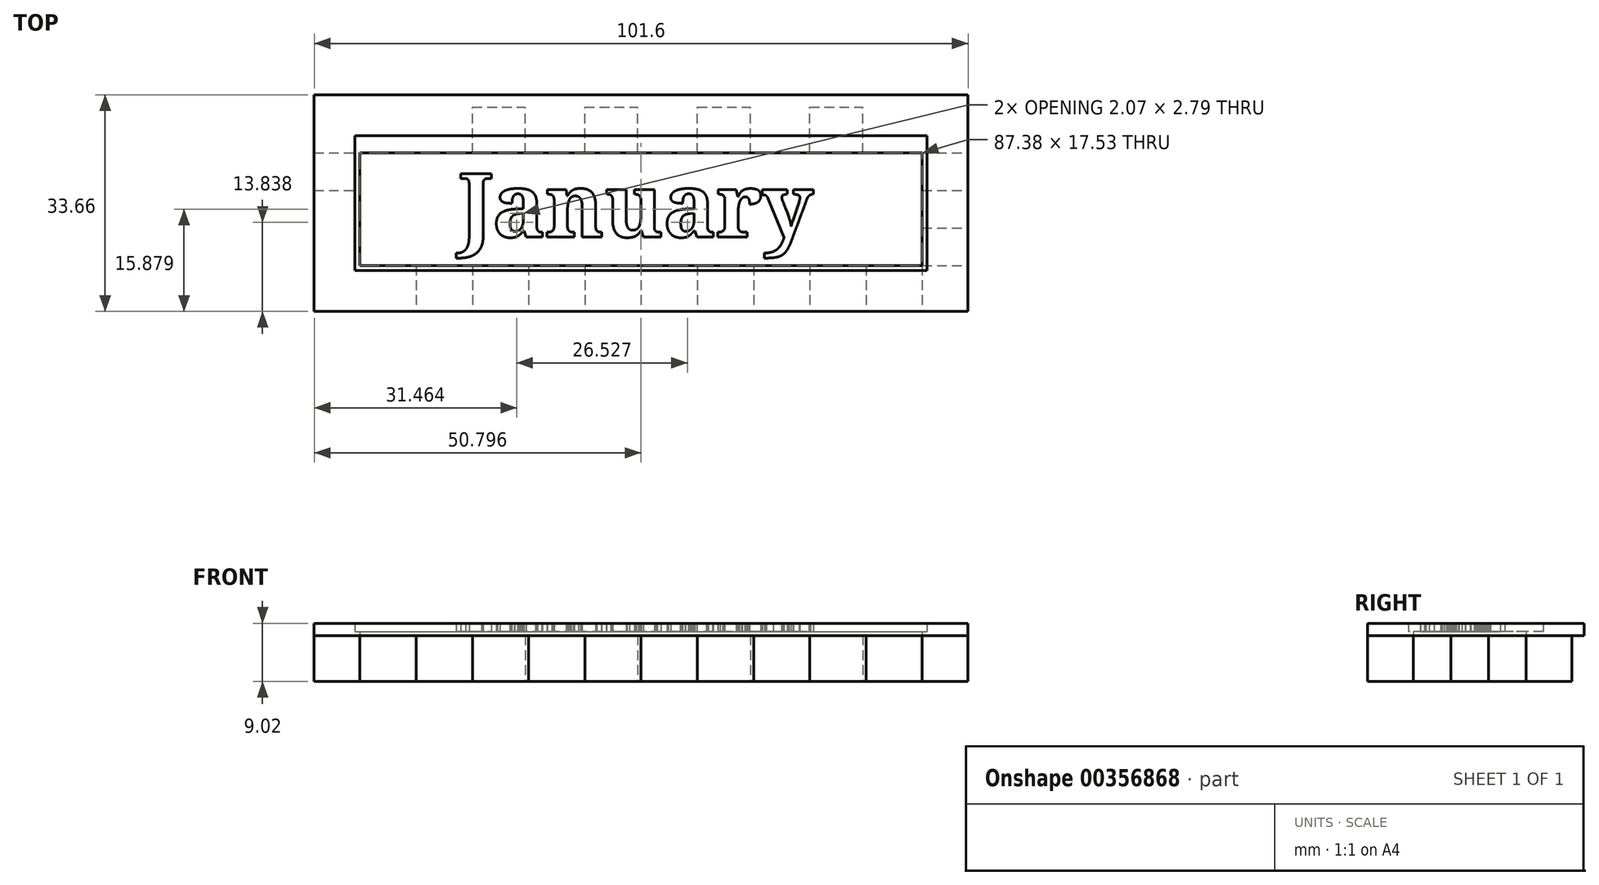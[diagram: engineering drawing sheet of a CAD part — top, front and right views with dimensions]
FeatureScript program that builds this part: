
annotation { "Feature Type Name" : "Feature", "Feature Type Description" : "" }
export const myFeature = defineFeature(function(context is Context, id is Id, definition is map)
    precondition{}
    {
        {
            var Q0;
            Q0=qCreatedBy(makeId("Top.planeOp"),FACE);
            var sketch = newSketch(context, id + "F0", { "sketchPlane" : qUnion([Q0])});
            skLineSegment(sketch, "E0.bottom", {"start": v(-52.12, 11.37) * mm, "end": v(49.48, 11.37) * mm});
            skLineSegment(sketch, "E0.top", {"start": v(-52.12, -20.38) * mm, "end": v(49.48, -20.38) * mm});
            skLineSegment(sketch, "E0.left", {"start": v(-52.12, 11.37) * mm, "end": v(-52.12, -20.38) * mm});
            skLineSegment(sketch, "E0.right", {"start": v(49.48, 11.37) * mm, "end": v(49.48, -20.38) * mm});
            skLineSegment(sketch, "E1.bottom", {"start": v(-52.12, 11.37) * mm, "end": v(-45.01, 11.37) * mm});
            skLineSegment(sketch, "E1.top", {"start": v(-52.12, 4.26) * mm, "end": v(-45.01, 4.26) * mm});
            skLineSegment(sketch, "E1.left", {"start": v(-52.12, 11.37) * mm, "end": v(-52.12, 4.26) * mm});
            skLineSegment(sketch, "E1.right", {"start": v(-45.01, 11.37) * mm, "end": v(-45.01, 4.26) * mm});
            skLineSegment(sketch, "E2.bottom", {"start": v(-45.01, 11.37) * mm, "end": v(-36.78, 11.37) * mm});
            skLineSegment(sketch, "E2.top", {"start": v(-45.01, 4.26) * mm, "end": v(-36.78, 4.26) * mm});
            skLineSegment(sketch, "E2.right", {"start": v(-36.78, 11.37) * mm, "end": v(-36.78, 4.26) * mm});
            skLineSegment(sketch, "E3.bottom", {"start": v(-36.78, 4.26) * mm, "end": v(-27.54, 4.26) * mm});
            skLineSegment(sketch, "E3.top", {"start": v(-36.78, 11.37) * mm, "end": v(-27.54, 11.37) * mm});
            skLineSegment(sketch, "E3.left", {"start": v(-36.78, 4.26) * mm, "end": v(-36.78, 11.37) * mm});
            skLineSegment(sketch, "E3.right", {"start": v(-27.54, 4.26) * mm, "end": v(-27.54, 11.37) * mm});
            skLineSegment(sketch, "E4.bottom", {"start": v(-27.54, 4.26) * mm, "end": v(-19.3, 4.26) * mm});
            skLineSegment(sketch, "E4.top", {"start": v(-27.54, 11.37) * mm, "end": v(-19.3, 11.37) * mm});
            skLineSegment(sketch, "E4.right", {"start": v(-19.3, 4.26) * mm, "end": v(-19.3, 11.37) * mm});
            skLineSegment(sketch, "E5.bottom", {"start": v(-19.3, 4.26) * mm, "end": v(-10.06, 4.26) * mm});
            skLineSegment(sketch, "E5.top", {"start": v(-19.3, 11.37) * mm, "end": v(-10.06, 11.37) * mm});
            skLineSegment(sketch, "E5.right", {"start": v(-10.06, 4.26) * mm, "end": v(-10.06, 11.37) * mm});
            skLineSegment(sketch, "E6.bottom", {"start": v(-10.06, 4.26) * mm, "end": v(-10.06, 4.26) * mm});
            skLineSegment(sketch, "E6.top", {"start": v(-10.06, 11.37) * mm, "end": v(-10.06, 11.37) * mm});
            skLineSegment(sketch, "E7.bottom", {"start": v(-10.06, 4.26) * mm, "end": v(-1.83, 4.26) * mm});
            skLineSegment(sketch, "E7.top", {"start": v(-10.06, 11.37) * mm, "end": v(-1.83, 11.37) * mm});
            skLineSegment(sketch, "E7.right", {"start": v(-1.83, 4.26) * mm, "end": v(-1.83, 11.37) * mm});
            skLineSegment(sketch, "E8.bottom", {"start": v(-1.83, 4.26) * mm, "end": v(7.41, 4.26) * mm});
            skLineSegment(sketch, "E8.top", {"start": v(-1.83, 11.37) * mm, "end": v(7.41, 11.37) * mm});
            skLineSegment(sketch, "E8.right", {"start": v(7.41, 4.26) * mm, "end": v(7.41, 11.37) * mm});
            skLineSegment(sketch, "E9.bottom", {"start": v(7.41, 4.26) * mm, "end": v(15.64, 4.26) * mm});
            skLineSegment(sketch, "E9.top", {"start": v(7.41, 11.37) * mm, "end": v(15.64, 11.37) * mm});
            skLineSegment(sketch, "E9.right", {"start": v(15.64, 4.26) * mm, "end": v(15.64, 11.37) * mm});
            skLineSegment(sketch, "E10.bottom", {"start": v(15.64, 4.26) * mm, "end": v(24.89, 4.26) * mm});
            skLineSegment(sketch, "E10.top", {"start": v(15.64, 11.37) * mm, "end": v(24.89, 11.37) * mm});
            skLineSegment(sketch, "E10.right", {"start": v(24.89, 4.26) * mm, "end": v(24.89, 11.37) * mm});
            skLineSegment(sketch, "E11.bottom", {"start": v(24.89, 4.26) * mm, "end": v(24.89, 4.26) * mm});
            skLineSegment(sketch, "E11.top", {"start": v(24.89, 11.37) * mm, "end": v(24.89, 11.37) * mm});
            skLineSegment(sketch, "E12.bottom", {"start": v(24.89, 4.26) * mm, "end": v(33.12, 4.26) * mm});
            skLineSegment(sketch, "E12.top", {"start": v(24.89, 11.37) * mm, "end": v(33.12, 11.37) * mm});
            skLineSegment(sketch, "E12.right", {"start": v(33.12, 4.26) * mm, "end": v(33.12, 11.37) * mm});
            skLineSegment(sketch, "E13.bottom", {"start": v(33.12, 4.26) * mm, "end": v(42.36, 4.26) * mm});
            skLineSegment(sketch, "E13.top", {"start": v(33.12, 11.37) * mm, "end": v(42.36, 11.37) * mm});
            skLineSegment(sketch, "E13.right", {"start": v(42.36, 4.26) * mm, "end": v(42.36, 11.37) * mm});
            skLineSegment(sketch, "E14.bottom", {"start": v(42.36, 4.26) * mm, "end": v(49.48, 4.26) * mm});
            skLineSegment(sketch, "E14.top", {"start": v(42.36, 11.37) * mm, "end": v(49.48, 11.37) * mm});
            skLineSegment(sketch, "E14.right", {"start": v(49.48, 4.26) * mm, "end": v(49.48, 11.37) * mm});
            skLineSegment(sketch, "E15.bottom", {"start": v(-52.12, -20.38) * mm, "end": v(-45.01, -20.38) * mm});
            skLineSegment(sketch, "E15.top", {"start": v(-52.12, -13.26) * mm, "end": v(-45.01, -13.26) * mm});
            skLineSegment(sketch, "E15.left", {"start": v(-52.12, -20.38) * mm, "end": v(-52.12, -13.26) * mm});
            skLineSegment(sketch, "E15.right", {"start": v(-45.01, -20.38) * mm, "end": v(-45.01, -13.26) * mm});
            skLineSegment(sketch, "E16.bottom", {"start": v(-45.01, -13.26) * mm, "end": v(-45.01, -13.26) * mm});
            skLineSegment(sketch, "E16.top", {"start": v(-45.01, -20.38) * mm, "end": v(-45.01, -20.38) * mm});
            skLineSegment(sketch, "E16.left", {"start": v(-45.01, -13.26) * mm, "end": v(-45.01, -20.38) * mm});
            skLineSegment(sketch, "E16.right", {"start": v(-45.01, -13.26) * mm, "end": v(-45.01, -20.38) * mm});
            skLineSegment(sketch, "E17.bottom", {"start": v(-45.01, -13.26) * mm, "end": v(-36.27, -13.26) * mm});
            skLineSegment(sketch, "E17.top", {"start": v(-45.01, -20.38) * mm, "end": v(-36.27, -20.38) * mm});
            skLineSegment(sketch, "E17.right", {"start": v(-36.27, -13.26) * mm, "end": v(-36.27, -20.38) * mm});
            skLineSegment(sketch, "E18.bottom", {"start": v(-36.27, -13.26) * mm, "end": v(-36.27, -13.26) * mm});
            skLineSegment(sketch, "E18.top", {"start": v(-36.27, -20.38) * mm, "end": v(-36.27, -20.38) * mm});
            skLineSegment(sketch, "E19.bottom", {"start": v(-36.27, -13.26) * mm, "end": v(-27.54, -13.26) * mm});
            skLineSegment(sketch, "E19.top", {"start": v(-36.27, -20.38) * mm, "end": v(-27.54, -20.38) * mm});
            skLineSegment(sketch, "E19.right", {"start": v(-27.54, -13.26) * mm, "end": v(-27.54, -20.38) * mm});
            skLineSegment(sketch, "E20.bottom", {"start": v(-27.54, -13.26) * mm, "end": v(-18.8, -13.26) * mm});
            skLineSegment(sketch, "E20.top", {"start": v(-27.54, -20.38) * mm, "end": v(-18.8, -20.38) * mm});
            skLineSegment(sketch, "E20.right", {"start": v(-18.8, -13.26) * mm, "end": v(-18.8, -20.38) * mm});
            skLineSegment(sketch, "E21.bottom", {"start": v(-18.8, -13.26) * mm, "end": v(-10.06, -13.26) * mm});
            skLineSegment(sketch, "E21.top", {"start": v(-18.8, -20.38) * mm, "end": v(-10.06, -20.38) * mm});
            skLineSegment(sketch, "E21.right", {"start": v(-10.06, -13.26) * mm, "end": v(-10.06, -20.38) * mm});
            skLineSegment(sketch, "E22.bottom", {"start": v(-10.06, -13.26) * mm, "end": v(-1.32, -13.26) * mm});
            skLineSegment(sketch, "E22.top", {"start": v(-10.06, -20.38) * mm, "end": v(-1.32, -20.38) * mm});
            skLineSegment(sketch, "E22.right", {"start": v(-1.32, -13.26) * mm, "end": v(-1.32, -20.38) * mm});
            skLineSegment(sketch, "E23.bottom", {"start": v(-1.32, -13.26) * mm, "end": v(7.41, -13.26) * mm});
            skLineSegment(sketch, "E23.top", {"start": v(-1.32, -20.38) * mm, "end": v(7.41, -20.38) * mm});
            skLineSegment(sketch, "E23.right", {"start": v(7.41, -13.26) * mm, "end": v(7.41, -20.38) * mm});
            skLineSegment(sketch, "E24.bottom", {"start": v(7.41, -13.26) * mm, "end": v(16.15, -13.26) * mm});
            skLineSegment(sketch, "E24.top", {"start": v(7.41, -20.38) * mm, "end": v(16.15, -20.38) * mm});
            skLineSegment(sketch, "E24.right", {"start": v(16.15, -13.26) * mm, "end": v(16.15, -20.38) * mm});
            skLineSegment(sketch, "E25.bottom", {"start": v(16.15, -13.26) * mm, "end": v(24.89, -13.26) * mm});
            skLineSegment(sketch, "E25.top", {"start": v(16.15, -20.38) * mm, "end": v(24.89, -20.38) * mm});
            skLineSegment(sketch, "E25.right", {"start": v(24.89, -13.26) * mm, "end": v(24.89, -20.38) * mm});
            skLineSegment(sketch, "E26.bottom", {"start": v(24.89, -13.26) * mm, "end": v(33.63, -13.26) * mm});
            skLineSegment(sketch, "E26.top", {"start": v(24.89, -20.38) * mm, "end": v(33.63, -20.38) * mm});
            skLineSegment(sketch, "E26.right", {"start": v(33.63, -13.26) * mm, "end": v(33.63, -20.38) * mm});
            skLineSegment(sketch, "E27.bottom", {"start": v(33.63, -13.26) * mm, "end": v(42.36, -13.26) * mm});
            skLineSegment(sketch, "E27.top", {"start": v(33.63, -20.38) * mm, "end": v(42.36, -20.38) * mm});
            skLineSegment(sketch, "E27.right", {"start": v(42.36, -13.26) * mm, "end": v(42.36, -20.38) * mm});
            skLineSegment(sketch, "E28.bottom", {"start": v(42.36, -13.26) * mm, "end": v(49.48, -13.26) * mm});
            skLineSegment(sketch, "E28.top", {"start": v(42.36, -20.38) * mm, "end": v(49.48, -20.38) * mm});
            skLineSegment(sketch, "E28.right", {"start": v(49.48, -13.26) * mm, "end": v(49.48, -20.38) * mm});
            skLineSegment(sketch, "E29.top", {"start": v(-52.12, -1.58) * mm, "end": v(-45.01, -1.58) * mm});
            skLineSegment(sketch, "E29.left", {"start": v(-52.12, 4.26) * mm, "end": v(-52.12, -1.58) * mm});
            skLineSegment(sketch, "E29.right", {"start": v(-45.01, 4.26) * mm, "end": v(-45.01, -1.58) * mm});
            skLineSegment(sketch, "E30.top", {"start": v(-52.12, -7.42) * mm, "end": v(-45.01, -7.42) * mm});
            skLineSegment(sketch, "E30.left", {"start": v(-52.12, -1.58) * mm, "end": v(-52.12, -7.42) * mm});
            skLineSegment(sketch, "E30.right", {"start": v(-45.01, -1.58) * mm, "end": v(-45.01, -7.42) * mm});
            skLineSegment(sketch, "E31.bottom", {"start": v(-45.01, -7.42) * mm, "end": v(-52.12, -7.42) * mm});
            skLineSegment(sketch, "E31.top", {"start": v(-45.01, -13.26) * mm, "end": v(-52.12, -13.26) * mm});
            skLineSegment(sketch, "E31.left", {"start": v(-45.01, -7.42) * mm, "end": v(-45.01, -13.26) * mm});
            skLineSegment(sketch, "E31.right", {"start": v(-52.12, -7.42) * mm, "end": v(-52.12, -13.26) * mm});
            skLineSegment(sketch, "E32.top", {"start": v(42.36, -1.58) * mm, "end": v(49.48, -1.58) * mm});
            skLineSegment(sketch, "E32.left", {"start": v(42.36, 4.26) * mm, "end": v(42.36, -1.58) * mm});
            skLineSegment(sketch, "E32.right", {"start": v(49.48, 4.26) * mm, "end": v(49.48, -1.58) * mm});
            skLineSegment(sketch, "E33.top", {"start": v(42.36, -7.42) * mm, "end": v(49.48, -7.42) * mm});
            skLineSegment(sketch, "E33.left", {"start": v(42.36, -1.58) * mm, "end": v(42.36, -7.42) * mm});
            skLineSegment(sketch, "E33.right", {"start": v(49.48, -1.58) * mm, "end": v(49.48, -7.42) * mm});
            skLineSegment(sketch, "E34.left", {"start": v(42.36, -7.42) * mm, "end": v(42.36, -13.26) * mm});
            skLineSegment(sketch, "E34.right", {"start": v(49.48, -7.42) * mm, "end": v(49.48, -13.26) * mm});
            skSolve(sketch);
        }
        {
            var Q0;
            Q0=makeQuery(id+"F0.imprint","IMPRINT",FACE,{"disambiguationData":[TD([[makeQuery(id+"F0.imprint","IMPRINT",EDGE,{"derivedFrom":sQuery(id+"F0.wireOp",EDGE,"E2.top")}),-1.0]])]});
            var Q1;
            Q1=makeQuery(id+"F0.imprint","IMPRINT",FACE,{"disambiguationData":[TD([[makeQuery(id+"F0.imprint","IMPRINT",EDGE,{"derivedFrom":sQuery(id+"F0.wireOp",EDGE,"E2.bottom")}),-1.0]])]});
            var Q2;
            Q2=makeQuery(id+"F0.imprint","IMPRINT",FACE,{"disambiguationData":[TD([[makeQuery(id+"F0.imprint","IMPRINT",EDGE,{"derivedFrom":sQuery(id+"F0.wireOp",EDGE,"E4.bottom")}),1.0]])]});
            var Q3;
            Q3=makeQuery(id+"F0.imprint","IMPRINT",FACE,{"disambiguationData":[TD([[makeQuery(id+"F0.imprint","IMPRINT",EDGE,{"derivedFrom":sQuery(id+"F0.wireOp",EDGE,"E7.bottom")}),1.0]])]});
            var Q4;
            Q4=makeQuery(id+"F0.imprint","IMPRINT",FACE,{"disambiguationData":[TD([[makeQuery(id+"F0.imprint","IMPRINT",EDGE,{"derivedFrom":sQuery(id+"F0.wireOp",EDGE,"E9.bottom")}),1.0]])]});
            var Q5;
            Q5=makeQuery(id+"F0.imprint","IMPRINT",FACE,{"disambiguationData":[TD([[makeQuery(id+"F0.imprint","IMPRINT",EDGE,{"derivedFrom":sQuery(id+"F0.wireOp",EDGE,"E12.bottom")}),1.0]])]});
            var Q6;
            Q6=makeQuery(id+"F0.imprint","IMPRINT",FACE,{"disambiguationData":[TD([[makeQuery(id+"F0.imprint","IMPRINT",EDGE,{"derivedFrom":sQuery(id+"F0.wireOp",EDGE,"E14.bottom")}),-1.0]])]});
            var Q7;
            Q7=makeQuery(id+"F0.imprint","IMPRINT",FACE,{"disambiguationData":[TD([[makeQuery(id+"F0.imprint","IMPRINT",EDGE,{"derivedFrom":sQuery(id+"F0.wireOp",EDGE,"E33.top")}),-1.0]])]});
            var Q8;
            Q8=makeQuery(id+"F0.imprint","IMPRINT",FACE,{"disambiguationData":[TD([[makeQuery(id+"F0.imprint","IMPRINT",EDGE,{"derivedFrom":sQuery(id+"F0.wireOp",EDGE,"E27.bottom")}),-1.0]])]});
            var Q9;
            Q9=makeQuery(id+"F0.imprint","IMPRINT",FACE,{"disambiguationData":[TD([[makeQuery(id+"F0.imprint","IMPRINT",EDGE,{"derivedFrom":sQuery(id+"F0.wireOp",EDGE,"E25.bottom")}),-1.0]])]});
            var Q10;
            Q10=makeQuery(id+"F0.imprint","IMPRINT",FACE,{"disambiguationData":[TD([[makeQuery(id+"F0.imprint","IMPRINT",EDGE,{"derivedFrom":sQuery(id+"F0.wireOp",EDGE,"E23.bottom")}),-1.0]])]});
            var Q11;
            Q11=makeQuery(id+"F0.imprint","IMPRINT",FACE,{"disambiguationData":[TD([[makeQuery(id+"F0.imprint","IMPRINT",EDGE,{"derivedFrom":sQuery(id+"F0.wireOp",EDGE,"E21.bottom")}),-1.0]])]});
            var Q12;
            Q12=makeQuery(id+"F0.imprint","IMPRINT",FACE,{"disambiguationData":[TD([[makeQuery(id+"F0.imprint","IMPRINT",EDGE,{"derivedFrom":sQuery(id+"F0.wireOp",EDGE,"E19.bottom")}),-1.0]])]});
            var Q13;
            Q13=makeQuery(id+"F0.imprint","IMPRINT",FACE,{"disambiguationData":[TD([[makeQuery(id+"F0.imprint","IMPRINT",EDGE,{"derivedFrom":sQuery(id+"F0.wireOp",EDGE,"E31.bottom")}),1.0]])]});
            var Q14;
            Q14=makeQuery(id+"F0.imprint","IMPRINT",FACE,{"disambiguationData":[TD([[makeQuery(id+"F0.imprint","IMPRINT",EDGE,{"derivedFrom":sQuery(id+"F0.wireOp",EDGE,"E1.top")}),-1.0]])]});
            extrude(context, id + "F1", {"entities" : qUnion([Q0, Q1, Q2, Q3, Q4, Q5, Q6, Q7, Q8, Q9, Q10, Q11, Q12, Q13, Q14]), "depth" : 7.11 * mm});
        }
        {
            var Q0;
            Q0=makeQuery(id+"F1.opExtrude","CAP_FACE",FACE,{"disambiguationData":[OSD([sQuery(id+"F0.wireOp",EDGE,"E2.bottom"),sQuery(id+"F0.wireOp",EDGE,"E1.right"),sQuery(id+"F0.wireOp",EDGE,"E3.bottom"),sQuery(id+"F0.wireOp",EDGE,"E3.left"),sQuery(id+"F0.wireOp",EDGE,"E4.top"),sQuery(id+"F0.wireOp",EDGE,"E3.right"),sQuery(id+"F0.wireOp",EDGE,"E5.bottom"),sQuery(id+"F0.wireOp",EDGE,"E4.right"),sQuery(id+"F0.wireOp",EDGE,"E6.top"),sQuery(id+"F0.wireOp",EDGE,"E5.right"),sQuery(id+"F0.wireOp",EDGE,"E7.bottom"),sQuery(id+"F0.wireOp",EDGE,"E5.right"),sQuery(id+"F0.wireOp",EDGE,"E8.top"),sQuery(id+"F0.wireOp",EDGE,"E7.right"),sQuery(id+"F0.wireOp",EDGE,"E9.bottom"),sQuery(id+"F0.wireOp",EDGE,"E8.right"),sQuery(id+"F0.wireOp",EDGE,"E10.top"),sQuery(id+"F0.wireOp",EDGE,"E9.right"),sQuery(id+"F0.wireOp",EDGE,"E11.bottom"),sQuery(id+"F0.wireOp",EDGE,"E10.right"),sQuery(id+"F0.wireOp",EDGE,"E12.top"),sQuery(id+"F0.wireOp",EDGE,"E10.right"),sQuery(id+"F0.wireOp",EDGE,"E13.bottom"),sQuery(id+"F0.wireOp",EDGE,"E12.right"),sQuery(id+"F0.wireOp",EDGE,"E16.bottom"),sQuery(id+"F0.wireOp",EDGE,"E17.top"),sQuery(id+"F0.wireOp",EDGE,"E16.left"),sQuery(id+"F0.wireOp",EDGE,"E18.bottom"),sQuery(id+"F0.wireOp",EDGE,"E17.right"),sQuery(id+"F0.wireOp",EDGE,"E19.top"),sQuery(id+"F0.wireOp",EDGE,"E17.right"),sQuery(id+"F0.wireOp",EDGE,"E20.bottom"),sQuery(id+"F0.wireOp",EDGE,"E19.right"),sQuery(id+"F0.wireOp",EDGE,"E21.top"),sQuery(id+"F0.wireOp",EDGE,"E20.right"),sQuery(id+"F0.wireOp",EDGE,"E22.bottom"),sQuery(id+"F0.wireOp",EDGE,"E21.right"),sQuery(id+"F0.wireOp",EDGE,"E23.top"),sQuery(id+"F0.wireOp",EDGE,"E22.right"),sQuery(id+"F0.wireOp",EDGE,"E24.bottom"),sQuery(id+"F0.wireOp",EDGE,"E23.right"),sQuery(id+"F0.wireOp",EDGE,"E25.top"),sQuery(id+"F0.wireOp",EDGE,"E24.right"),sQuery(id+"F0.wireOp",EDGE,"E26.bottom"),sQuery(id+"F0.wireOp",EDGE,"E25.right"),sQuery(id+"F0.wireOp",EDGE,"E27.top"),sQuery(id+"F0.wireOp",EDGE,"E26.right"),sQuery(id+"F0.wireOp",EDGE,"E27.right"),sQuery(id+"F0.wireOp",EDGE,"E1.top"),sQuery(id+"F0.wireOp",EDGE,"E29.left"),sQuery(id+"F0.wireOp",EDGE,"E29.top"),sQuery(id+"F0.wireOp",EDGE,"E30.right"),sQuery(id+"F0.wireOp",EDGE,"E31.bottom"),sQuery(id+"F0.wireOp",EDGE,"E31.top"),sQuery(id+"F0.wireOp",EDGE,"E31.right"),sQuery(id+"F0.wireOp",EDGE,"E14.bottom"),sQuery(id+"F0.wireOp",EDGE,"E32.right"),sQuery(id+"F0.wireOp",EDGE,"E32.top"),sQuery(id+"F0.wireOp",EDGE,"E33.left"),sQuery(id+"F0.wireOp",EDGE,"E33.top"),sQuery(id+"F0.wireOp",EDGE,"E28.bottom"),sQuery(id+"F0.wireOp",EDGE,"E34.right")])],"isStart":false});
            var sketch = newSketch(context, id + "F2", { "sketchPlane" : qUnion([Q0])});
            skLineSegment(sketch, "E35.bottom", {"start": v(-52.12, -20.38) * mm, "end": v(-45.01, -20.38) * mm});
            skLineSegment(sketch, "E35.top", {"start": v(-52.12, 13.28) * mm, "end": v(-45.01, 13.28) * mm});
            skLineSegment(sketch, "E35.left", {"start": v(-52.12, -20.38) * mm, "end": v(-52.12, 13.28) * mm});
            skLineSegment(sketch, "E35.right", {"start": v(-45.01, -20.38) * mm, "end": v(-45.01, 13.28) * mm});
            skLineSegment(sketch, "E36.bottom", {"start": v(-52.12, -20.38) * mm, "end": v(49.48, -20.38) * mm});
            skLineSegment(sketch, "E36.top", {"start": v(-52.12, -13.26) * mm, "end": v(49.48, -13.26) * mm});
            skLineSegment(sketch, "E36.left", {"start": v(-52.12, -20.38) * mm, "end": v(-52.12, -13.26) * mm});
            skLineSegment(sketch, "E36.right", {"start": v(49.48, -20.38) * mm, "end": v(49.48, -13.26) * mm});
            skPoint(sketch, "E37.oppositeSnap0", {"position": v(42.36, -4.5) * mm});
            skLineSegment(sketch, "E37.bottom", {"start": v(49.48, -20.38) * mm, "end": v(42.36, -20.38) * mm});
            skLineSegment(sketch, "E37.top", {"start": v(49.48, 13.28) * mm, "end": v(42.36, 13.28) * mm});
            skLineSegment(sketch, "E37.left", {"start": v(49.48, -20.38) * mm, "end": v(49.48, 13.28) * mm});
            skLineSegment(sketch, "E37.right", {"start": v(42.36, -20.38) * mm, "end": v(42.36, 13.28) * mm});
            skLineSegment(sketch, "E38.bottom", {"start": v(-52.12, 13.28) * mm, "end": v(49.48, 13.28) * mm});
            skLineSegment(sketch, "E38.top", {"start": v(-52.12, 4.26) * mm, "end": v(49.48, 4.26) * mm});
            skLineSegment(sketch, "E38.left", {"start": v(-52.12, 13.28) * mm, "end": v(-52.12, 4.26) * mm});
            skLineSegment(sketch, "E38.right", {"start": v(49.48, 13.28) * mm, "end": v(49.48, 4.26) * mm});
            skSolve(sketch);
        }
        {
            var Q0;
            Q0=qSketchRegion(id+"F2",true);
            var Q1;
            {var subQ5=sQuery(id+"F2.wireOp",EDGE,"E36.top");var subQ10=sQuery(id+"F2.wireOp",EDGE,"E35.right");var subQ12=makeQuery(id+"F2.imprint","INTERSECT",VERTEX,{"derivedFrom":[makeQuery(id+"F1.opExtrude","CAP_EDGE",EDGE,{"disambiguationData":[OSD([sQuery(id+"F0.wireOp",EDGE,"E31.bottom")])],"isStart":false}),subQ10]});var subQ24=makeQuery(id+"F2.imprint","INTERSECT",VERTEX,{"derivedFrom":[subQ10,subQ5]});Q1=makeQuery(id+"F2.imprint","IMPRINT",FACE,{"disambiguationData":[TD([[makeQuery(id+"F2.imprint","IMPRINT",EDGE,{"disambiguationData":[TD([[subQ12,1.0],[subQ24,-1.0]])],"derivedFrom":subQ10}),-1.0]])]});}
            extrude(context, id + "F3", {"entities" : qUnion([Q0, Q1]), "depth" : 0.64 * mm});
        }
        {
            var Q0;
            Q0=makeQuery(id+"F3.opExtrude","CAP_FACE",FACE,{"disambiguationData":[OSD([sQuery(id+"F2.wireOp",EDGE,"E35.left"),sQuery(id+"F2.wireOp",EDGE,"E36.bottom"),sQuery(id+"F2.wireOp",EDGE,"E36.left"),sQuery(id+"F2.wireOp",EDGE,"E37.bottom"),sQuery(id+"F2.wireOp",EDGE,"E37.left"),sQuery(id+"F2.wireOp",EDGE,"E38.bottom"),sQuery(id+"F2.wireOp",EDGE,"E38.left"),sQuery(id+"F2.wireOp",EDGE,"E38.right")])],"isStart":false});
            var sketch = newSketch(context, id + "F4", { "sketchPlane" : qUnion([Q0])});
            skLineSegment(sketch, "E39.bottom", {"start": v(-52.12, 13.28) * mm, "end": v(49.48, 13.28) * mm});
            skLineSegment(sketch, "E39.top", {"start": v(-52.12, 6.93) * mm, "end": v(49.48, 6.93) * mm});
            skLineSegment(sketch, "E39.left", {"start": v(-52.12, 13.28) * mm, "end": v(-52.12, 6.93) * mm});
            skLineSegment(sketch, "E39.right", {"start": v(49.48, 13.28) * mm, "end": v(49.48, 6.93) * mm});
            skLineSegment(sketch, "E40.bottom", {"start": v(-52.12, 13.28) * mm, "end": v(-45.77, 13.28) * mm});
            skLineSegment(sketch, "E40.top", {"start": v(-52.12, -20.38) * mm, "end": v(-45.77, -20.38) * mm});
            skLineSegment(sketch, "E40.left", {"start": v(-52.12, 13.28) * mm, "end": v(-52.12, -20.38) * mm});
            skLineSegment(sketch, "E40.right", {"start": v(-45.77, 13.28) * mm, "end": v(-45.77, -20.38) * mm});
            skLineSegment(sketch, "E41.bottom", {"start": v(-52.12, -14.03) * mm, "end": v(49.48, -14.03) * mm});
            skLineSegment(sketch, "E41.top", {"start": v(-52.12, -20.38) * mm, "end": v(49.48, -20.38) * mm});
            skLineSegment(sketch, "E41.left", {"start": v(-52.12, -14.03) * mm, "end": v(-52.12, -20.38) * mm});
            skLineSegment(sketch, "E41.right", {"start": v(49.48, -14.03) * mm, "end": v(49.48, -20.38) * mm});
            skLineSegment(sketch, "E42.bottom", {"start": v(49.48, -20.38) * mm, "end": v(43.13, -20.38) * mm});
            skLineSegment(sketch, "E42.top", {"start": v(49.48, 13.28) * mm, "end": v(43.13, 13.28) * mm});
            skLineSegment(sketch, "E42.left", {"start": v(49.48, -20.38) * mm, "end": v(49.48, 13.28) * mm});
            skLineSegment(sketch, "E42.right", {"start": v(43.13, -20.38) * mm, "end": v(43.13, 13.28) * mm});
            skSolve(sketch);
        }
        {
            var Q0;
            Q0=qSketchRegion(id+"F4",true);
            extrude(context, id + "F5", {"entities" : qUnion([Q0]), "operationType" : NewBodyOperationType.ADD, "depth" : 1.27 * mm});
        }
        {
            var Q0;
            Q0=makeQuery(id+"F3.opExtrude","CAP_FACE",FACE,{"disambiguationData":[OSD([sQuery(id+"F2.wireOp",EDGE,"E35.left"),sQuery(id+"F2.wireOp",EDGE,"E36.bottom"),sQuery(id+"F2.wireOp",EDGE,"E36.left"),sQuery(id+"F2.wireOp",EDGE,"E37.bottom"),sQuery(id+"F2.wireOp",EDGE,"E37.left"),sQuery(id+"F2.wireOp",EDGE,"E38.bottom"),sQuery(id+"F2.wireOp",EDGE,"E38.left"),sQuery(id+"F2.wireOp",EDGE,"E38.right")])],"isStart":false});
            var sketch = newSketch(context, id + "F6", { "sketchPlane" : qUnion([Q0])});
            skText(sketch, "E43", { "text": "January", "fontName": "NotoSerif-Bold.ttf"});
            const initialGuessF6  = {"E43": [-0.02949, -0.0088, 1, 0, 0.00988]};
            skSetInitialGuess(sketch, initialGuessF6);
            skSolve(sketch);
        }
        {
            var Q0;
            Q0 = qSketchRegion(id + "F6", true);
            extrude(context, id + "F7", {"entities" : qUnion([Q0]), "operationType" : NewBodyOperationType.ADD, "depth" : 1.27 * mm});
        }
    });
